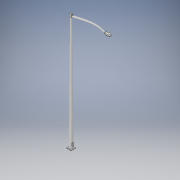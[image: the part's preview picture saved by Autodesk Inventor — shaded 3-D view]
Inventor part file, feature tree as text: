
AUTODESK INVENTOR PART (.ipt)
format: ipt  version: 2018 (Build 220112000, 112)  size: 475,648 bytes
history: native  units: in
note: dims shown in document units (in); Inventor stores cm internally (conversion verified against a paired STEP export)
features: sketch x8, extrude x4, plane x3, projected_geometry x2, revolve x1, loft x1, fillet x1
ambient origin geometry x8: Origin, YZ Plane, XZ Plane, XY Plane, X Axis, Y Axis, Z Axis, Center Point
bodies: Solid1 (feature_tree)
feature tree (20):
  revolve  "Revolution1"  [1 undecoded]
  plane  "Work Plane1"
  extrude  "Extrusion1"  Depth=2.0in
  sketch  "Sketch3"  dims[d4=0.25in d5=0.25in]
  sketch  "Sketch4"  dims[d6=2.0in d7=2.0in d8=0.3in]
  plane  "Work Plane2"
  loft  "Loft1"
  plane  "Work Plane3"
  extrude  "Extrusion2"  Depth=2.0in
  fillet  "Fillet1"  Radius=0.3in
  extrude  "Extrusion3"  Depth=1.1in
  extrude  "Extrusion4"  Depth=0.125in
  sketch  "Sketch1"  dims[d0=6.0in d1=1.0in]
  sketch  "Sketch2"  dims[d2=2.0in d3=300.0in]
  projected_geometry  "Projected Loop1"
  sketch  "Sketch5"  dims[d9=0.5in d10=1.1in]
  sketch  "Sketch6"  dims[d11=1.5in d12=0.125in]
  sketch  "Sketch7"  dims[d13=0.125in]
  sketch  "Sketch8"  dims[d14=0.6604in d15=0.9813in d16=1.8221in d17=0.0in d18=90.0deg d19=2.0in d20=5.0in d21=2.0in d22=0.5in d23=1.0in d24=0.0in d25=4.0in d26=2.5in d27=2.5in d28=84.0in d29=6.0in d30=53.0in d31=11.0in d32=10.0in d33=1.0in d34=3.0in d35=11.0in d36=87.0in d37=3.0in d38=0.0in d39=90.0deg d40=0.0in d41=90.0deg d42=0.0in d43=90.0deg d44=301.5in d45=3.0in d46=16.0in d47=6.0in d48=14.5in d49=5.0in d50=3.75in d51=4.0in d52=0.0in d53=1.5in d54=1.0in d55=0.0in d56=2.0in d57=6.0in d58=6.0in d59=5.0in d60=0.0in]
  projected_geometry  "Projected Loop2"
note: 1 required parameter value undecoded (feature->parameter linkage not recoverable at this tier; creation-order binding heuristic only, values carry confidence <= 0.55)
